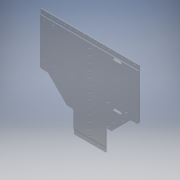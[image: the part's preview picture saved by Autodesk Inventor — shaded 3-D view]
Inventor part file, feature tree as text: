
AUTODESK INVENTOR PART (.ipt)
format: ipt  version: 2016 (Build 200138000, 138)  size: 386,560 bytes
history: native  units: in
note: dims shown in document units (in); Inventor stores cm internally (conversion verified against a paired STEP export)
features: sketch x9, reference x7, hole x6, extrude x4, projected_geometry x4, fillet x1, plane x1
ambient origin geometry x8: Origin, YZ Plane, XZ Plane, XY Plane, X Axis, Y Axis, Z Axis, Center Point
bodies: Solid1 (feature_tree)
feature tree (32):
  extrude  "Extrusion1"  Depth=14.5in
  extrude  "Extrusion2"  Depth=13.0in
  extrude  "Extrusion3"  Depth=0.1in TaperAngle=0.0deg
  fillet  "Fillet1"  Radius=0.5in
  hole  "Hole2"  [1 undecoded]
  hole  "Hole3"  [1 undecoded]
  sketch  "Sketch7"  dims[d47=0.25in d48=0.125in]
  extrude  "Extrusion4"  TaperAngle=45.0deg  [1 undecoded]
  hole  "Hole4"  [1 undecoded]
  hole  "Hole6"  [1 undecoded]
  plane  "Work Plane1"
  sketch  "Sketch8"  dims[d49=1.0in d50=45.0deg]
  hole  "Hole7"  [1 undecoded]
  hole  "Hole8"  [1 undecoded]
  sketch  "Sketch10"  dims[d58=0.19in d59=0.75in d60=0.375in d61=0.25in d62=0.5635in d63=1.0in d64=0.8108in d76=1.0in d77=0.0in d78=0.27in d79=0.75in d80=0.375in d81=0.25in d82=0.5635in d83=1.0in d84=0.8108in d92=0.201in d93=0.75in d94=0.375in d95=0.25in d96=0.5635in d97=1.0in d98=0.8108in d100=0.5in d101=0.25in d102=0.75in d103=5.9055in d105=1.0in d106=0.3937in d108=1.0in d110=1.9685in d112=1.0in d113=0.3937in d115=1.0in d118=2.85in d119=0.52in d120=0.19in d121=1.0in d122=0.925in d123=0.19in d124=1.0in d127=0.25in d128=3.4in d129=6.5in d130=0.201in d131=0.75in d132=0.507in d133=0.25in d134=0.5635in d135=1.0in d136=0.8108in d137=0.169in d138=0.75in d139=0.507in d140=0.25in d141=0.5635in d142=1.0in d143=0.8108in]
  sketch  "Sketch1"  dims[d0=15.5in d1=14.5in]
  sketch  "Sketch2"  dims[d2=0.25in d3=0.0in d4=13.0in]
  sketch  "Sketch3"  dims[d5=0.75in d6=0.1in d7=0.0in d9=0.5in d10=0.0in]
  sketch  "Sketch5"  dims[d27=0.25in]
  sketch  "Sketch6"  dims[d32=0.163in d33=0.75in d34=0.375in d35=0.25in d36=0.5635in d37=1.0in d38=0.8108in d45=45.0deg]
  reference  "Reference12"
  reference  "Reference13"
  reference  "Reference14"
  reference  "Reference15"
  reference  "Reference16"
  projected_geometry  "Projected Loop2"
  projected_geometry  "Projected Loop3"
  sketch  "Sketch9"  dims[d51=3.0in]
  reference  "Reference26"
  reference  "Reference27"
  projected_geometry  "Projected Loop4"
  projected_geometry  "Projected Loop5"
note: 7 required parameter values undecoded (feature->parameter linkage not recoverable at this tier; creation-order binding heuristic only, values carry confidence <= 0.55)
